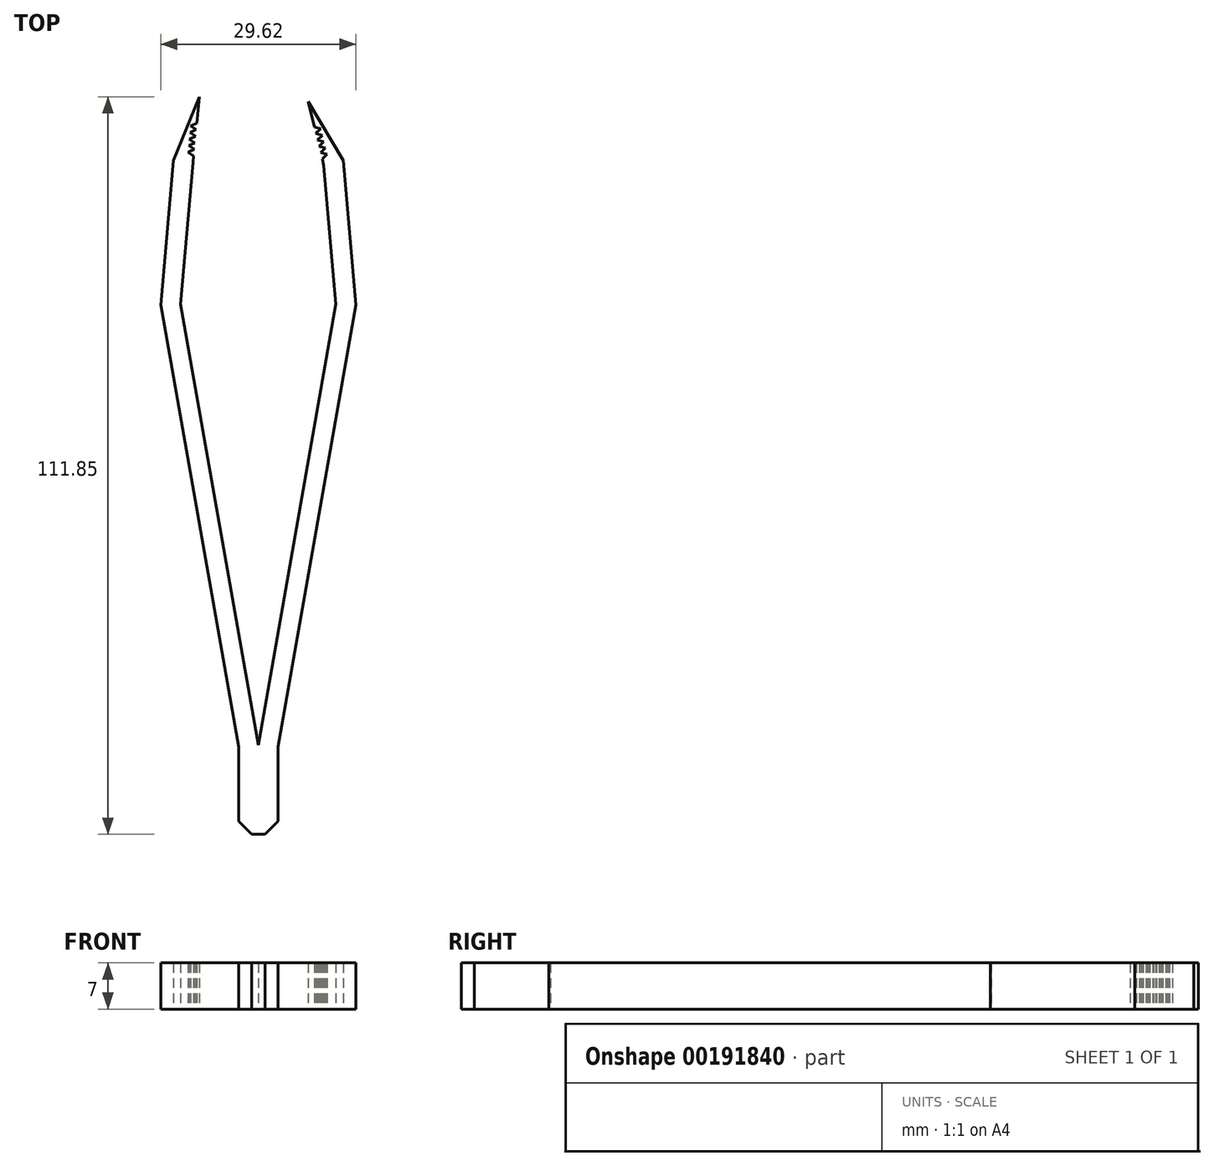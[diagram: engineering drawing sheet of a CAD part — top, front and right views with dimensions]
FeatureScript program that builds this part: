
annotation { "Feature Type Name" : "Feature", "Feature Type Description" : "" }
export const myFeature = defineFeature(function(context is Context, id is Id, definition is map)
    precondition{}
    {
        {
            var Q0;
            Q0=qCreatedBy(makeId("Top.planeOp"),FACE);
            var sketch = newSketch(context, id + "F0", { "sketchPlane" : qUnion([Q0])});
            skLineSegment(sketch, "E0.bottom", {"start": v(-2.83, -45.39) * mm, "end": v(3.17, -45.39) * mm});
            skLineSegment(sketch, "E0.top", {"start": v(-2.83, -32.1) * mm, "end": v(3.17, -32.1) * mm});
            skLineSegment(sketch, "E0.left", {"start": v(-2.83, -45.39) * mm, "end": v(-2.83, -32.1) * mm});
            skLineSegment(sketch, "E0.right", {"start": v(3.17, -45.39) * mm, "end": v(3.17, -32.1) * mm});
            skLineSegment(sketch, "E1", {"start": v(3.17, -32.1) * mm, "end": v(14.98, 34.87) * mm});
            skLineSegment(sketch, "E2", {"start": v(14.98, 34.87) * mm, "end": v(13.06, 56.79) * mm});
            skLineSegment(sketch, "E3.0", {"start": v(0.17, -31.83) * mm, "end": v(11.95, 35) * mm});
            skLineSegment(sketch, "E4", {"start": v(-2.83, -32.1) * mm, "end": v(-14.64, 34.87) * mm});
            skLineSegment(sketch, "E5.0", {"start": v(0.17, -31.83) * mm, "end": v(-11.62, 35) * mm});
            skLineSegment(sketch, "E6", {"start": v(-14.64, 34.87) * mm, "end": v(-12.72, 56.79) * mm});
            skLineSegment(sketch, "E7.0", {"start": v(-11.62, 35) * mm, "end": v(-9.74, 56.5) * mm});
            skLineSegment(sketch, "E8.0", {"start": v(11.95, 35) * mm, "end": v(10.11, 56.06) * mm});
            skLineSegment(sketch, "E9", {"start": v(-9.74, 56.5) * mm, "end": v(-12.72, 56.79) * mm});
            skLineSegment(sketch, "E10", {"start": v(10.11, 56.06) * mm, "end": v(13.06, 56.79) * mm});
            skLineSegment(sketch, "E11", {"start": v(-9.74, 56.5) * mm, "end": v(-9.64, 57.5) * mm});
            skLineSegment(sketch, "E12", {"start": v(-8.78, 66.46) * mm, "end": v(-12.72, 56.79) * mm});
            skLineSegment(sketch, "E13", {"start": v(10.11, 56.06) * mm, "end": v(7.71, 65.77) * mm});
            skLineSegment(sketch, "E14", {"start": v(7.71, 65.77) * mm, "end": v(13.06, 56.79) * mm});
            skPoint(sketch, "E15", {"position": v(-9.64, 57.5) * mm});
            skPoint(sketch, "E16", {"position": v(-9.54, 58.5) * mm});
            skPoint(sketch, "E17", {"position": v(-9.45, 59.49) * mm});
            skPoint(sketch, "E18", {"position": v(-9.35, 60.49) * mm});
            skPoint(sketch, "E19", {"position": v(-9.26, 61.48) * mm});
            skPoint(sketch, "E20", {"position": v(-9.16, 62.48) * mm});
            skPoint(sketch, "E21", {"position": v(-9.07, 63.47) * mm});
            skPoint(sketch, "E22", {"position": v(-8.97, 64.47) * mm});
            skLineSegment(sketch, "E23", {"start": v(-9.64, 57.5) * mm, "end": v(-10.45, 58.08) * mm});
            skLineSegment(sketch, "E24", {"start": v(-10.45, 58.08) * mm, "end": v(-9.54, 58.5) * mm});
            skLineSegment(sketch, "E25", {"start": v(-9.45, 59.49) * mm, "end": v(-10.36, 59.07) * mm});
            skLineSegment(sketch, "E26", {"start": v(-10.36, 59.07) * mm, "end": v(-9.54, 58.5) * mm});
            skLineSegment(sketch, "E27", {"start": v(-9.45, 59.49) * mm, "end": v(-10.26, 60.07) * mm});
            skLineSegment(sketch, "E28", {"start": v(-10.26, 60.07) * mm, "end": v(-9.35, 60.49) * mm});
            skLineSegment(sketch, "E29", {"start": v(-9.35, 60.49) * mm, "end": v(-10.17, 61.07) * mm});
            skLineSegment(sketch, "E30", {"start": v(-10.17, 61.07) * mm, "end": v(-9.26, 61.48) * mm});
            skLineSegment(sketch, "E31", {"start": v(-9.26, 61.48) * mm, "end": v(-10.07, 62.06) * mm});
            skLineSegment(sketch, "E32", {"start": v(-10.07, 62.06) * mm, "end": v(-9.16, 62.48) * mm});
            skLineSegment(sketch, "E33.trimOffspring", {"start": v(-9.16, 62.48) * mm, "end": v(-8.78, 66.46) * mm});
            skPoint(sketch, "E34", {"position": v(9.87, 57.03) * mm});
            skPoint(sketch, "E35", {"position": v(9.63, 58) * mm});
            skPoint(sketch, "E36", {"position": v(9.4, 58.97) * mm});
            skPoint(sketch, "E37", {"position": v(9.15, 59.94) * mm});
            skPoint(sketch, "E38", {"position": v(8.91, 60.91) * mm});
            skPoint(sketch, "E39", {"position": v(8.67, 61.88) * mm});
            skLineSegment(sketch, "E40", {"start": v(9.87, 57.03) * mm, "end": v(10.6, 57.72) * mm});
            skLineSegment(sketch, "E41", {"start": v(10.6, 57.72) * mm, "end": v(9.63, 58) * mm});
            skLineSegment(sketch, "E42", {"start": v(9.63, 58) * mm, "end": v(10.35, 58.7) * mm});
            skLineSegment(sketch, "E43", {"start": v(10.35, 58.7) * mm, "end": v(9.4, 58.97) * mm});
            skLineSegment(sketch, "E44", {"start": v(9.4, 58.97) * mm, "end": v(10.11, 59.67) * mm});
            skLineSegment(sketch, "E45", {"start": v(10.11, 59.67) * mm, "end": v(9.15, 59.94) * mm});
            skLineSegment(sketch, "E46", {"start": v(9.15, 59.94) * mm, "end": v(9.87, 60.64) * mm});
            skLineSegment(sketch, "E47", {"start": v(9.87, 60.64) * mm, "end": v(8.91, 60.91) * mm});
            skLineSegment(sketch, "E48", {"start": v(8.91, 60.91) * mm, "end": v(9.63, 61.6) * mm});
            skLineSegment(sketch, "E49", {"start": v(9.63, 61.6) * mm, "end": v(8.67, 61.88) * mm});
            skSolve(sketch);
        }
        {
            var Q0;
            Q0=makeQuery(id+"F0.imprint","IMPRINT",FACE,{"disambiguationData":[TD([[makeQuery(id+"F0.imprint","IMPRINT",EDGE,{"derivedFrom":sQuery(id+"F0.wireOp",EDGE,"E9")}),-1.0]])]});
            var Q1;
            Q1=makeQuery(id+"F0.imprint","IMPRINT",FACE,{"disambiguationData":[TD([[makeQuery(id+"F0.imprint","IMPRINT",EDGE,{"derivedFrom":sQuery(id+"F0.wireOp",EDGE,"E0.top")}),1.0]])]});
            var Q2;
            Q2=makeQuery(id+"F0.imprint","IMPRINT",FACE,{"disambiguationData":[TD([[makeQuery(id+"F0.imprint","IMPRINT",EDGE,{"derivedFrom":sQuery(id+"F0.wireOp",EDGE,"E0.bottom")}),1.0]])]});
            var Q3;
            Q3=makeQuery(id+"F0.imprint","IMPRINT",FACE,{"disambiguationData":[TD([[makeQuery(id+"F0.imprint","IMPRINT",EDGE,{"derivedFrom":sQuery(id+"F0.wireOp",EDGE,"E10")}),1.0]])]});
            extrude(context, id + "F1", {"entities" : qUnion([Q0, Q1, Q2, Q3]), "depth" : 7 * mm});
        }
        {
            var Q0;
            Q0=makeQuery(id+"F1.opExtrude","SWEPT_EDGE",EDGE,{"disambiguationData":[OSD([sQuery(id+"F0.wireOp",EDGE,"E0.bottom"),sQuery(id+"F0.wireOp",EDGE,"E0.left")])]});
            var Q1;
            Q1=makeQuery(id+"F1.opExtrude","SWEPT_EDGE",EDGE,{"disambiguationData":[OSD([sQuery(id+"F0.wireOp",EDGE,"E0.bottom"),sQuery(id+"F0.wireOp",EDGE,"E0.right")])]});
            chamfer(context, id + "F2", {"entities" : qUnion([Q0, Q1]), "width" : 2 * mm, "tangentPropagation" : true});
        }
    });
